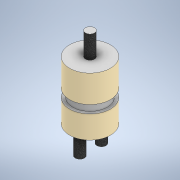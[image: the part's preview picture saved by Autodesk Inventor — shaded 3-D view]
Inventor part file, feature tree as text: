
AUTODESK INVENTOR PART (.ipt)
format: ipt  version: 2021 (Build 250183000, 183)  size: 130,560 bytes
history: native  units: mm
features: extrude x5, sketch x5
ambient origin geometry x8: Origin, YZ Plane, XZ Plane, XY Plane, X Axis, Y Axis, Z Axis, Center Point
bodies: Solid1 (feature_tree)
feature tree (10):
  extrude  "Extrusion1"  Depth=25.0mm TaperAngle=0.0deg
  extrude  "Extrusion2"  Depth=30.0mm TaperAngle=0.0deg
  extrude  "Extrusion3"  Depth=25.0mm TaperAngle=0.0deg
  extrude  "Extrusion4"  [1 undecoded]
  extrude  "Extrusion5"  [1 undecoded]
  sketch  "Sketch1"  dims[d0=45.0mm d1=25.0mm d2=0.0mm]
  sketch  "Sketch2"  dims[d3=9.0mm d4=0.0mm d5=30.0mm d6=0.0mm]
  sketch  "Sketch3"  dims[d7=10.0mm d8=25.0mm d9=0.0mm]
  sketch  "Sketch4"  dims[d10=25.0mm d11=0.0mm]
  sketch  "Sketch5"
note: 2 required parameter values undecoded (feature->parameter linkage not recoverable at this tier; creation-order binding heuristic only, values carry confidence <= 0.55)
